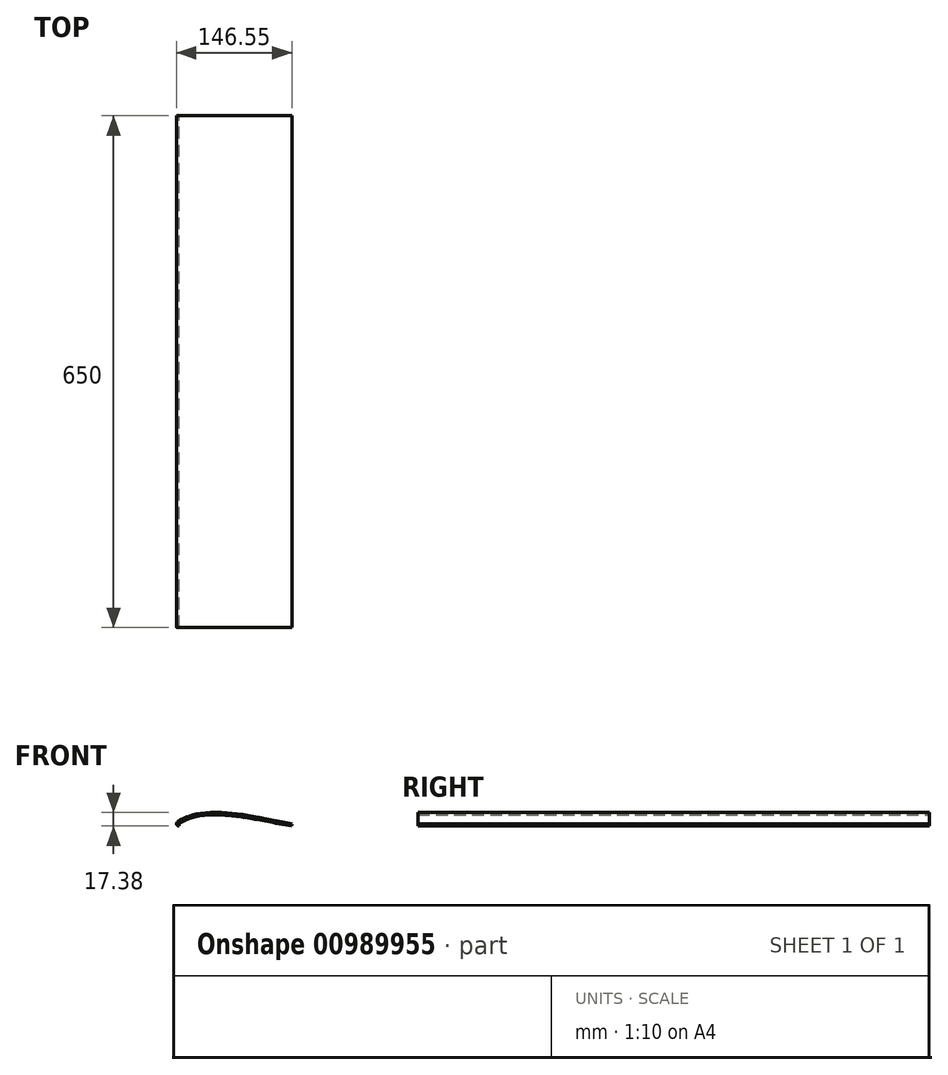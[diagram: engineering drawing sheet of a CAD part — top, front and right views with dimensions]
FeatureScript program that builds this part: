
annotation { "Feature Type Name" : "Feature", "Feature Type Description" : "" }
export const myFeature = defineFeature(function(context is Context, id is Id, definition is map)
    precondition{}
    {
        {
            var Q0;
            Q0=qCreatedBy(makeId("Front.planeOp"),FACE);
            var sketch = newSketch(context, id + "F0", { "sketchPlane" : qUnion([Q0])});
            skLineSegment(sketch, "E0", {"start": v(0, 0) * mm, "end": v(102, 0) * mm});
            skLineSegment(sketch, "E1.bottom", {"start": v(26, 0) * mm, "end": v(69, 0) * mm});
            skLineSegment(sketch, "E1.top", {"start": v(26, 10) * mm, "end": v(69, 10) * mm, "construction": true});
            skLineSegment(sketch, "E1.left", {"start": v(26, 0) * mm, "end": v(26, 10) * mm, "construction": true});
            skLineSegment(sketch, "E1.right", {"start": v(69, 0) * mm, "end": v(69, 10) * mm, "construction": true});
            skLineSegment(sketch, "E2", {"start": v(102, 0) * mm, "end": v(127, 0) * mm});
            skLineSegment(sketch, "E3.bottom", {"start": v(9, 0) * mm, "end": v(26, 0) * mm});
            skLineSegment(sketch, "E3.top", {"start": v(9, 5) * mm, "end": v(26, 5) * mm, "construction": true});
            skLineSegment(sketch, "E3.left", {"start": v(9, 0) * mm, "end": v(9, 5) * mm, "construction": true});
            skLineSegment(sketch, "E3.right", {"start": v(26, 0) * mm, "end": v(26, 5) * mm});
            skFitSpline(sketch, "E4", {"points": [v(0, 0) * mm, v(9, 5) * mm, v(26, 10) * mm, v(69, 10) * mm, v(127, 0) * mm], "startDerivative": vector(100.72, 59.29) * mm, "endDerivative": vector(193.95, -38.05) * mm});
            skLineSegment(sketch, "E5", {"start": v(0, 0) * mm, "end": v(0, -3) * mm});
            skLineSegment(sketch, "E6", {"start": v(0, -3) * mm, "end": v(143, -3) * mm});
            skLineSegment(sketch, "E7", {"start": v(143, -3) * mm, "end": v(127, 0) * mm});
            skLineSegment(sketch, "E8", {"start": v(143, -3) * mm, "end": v(143.55, -0.05) * mm});
            skFitSpline(sketch, "E9", {"points": [v(143.55, -0.05) * mm, v(69.31, 12.98) * mm, v(25.51, 12.96) * mm, v(7.77, 7.74) * mm, v(-1.5, 2.6) * mm], "startDerivative": vector(-307.51, 59.8) * mm, "endDerivative": vector(-155.36, -89.7) * mm});
            skArc(sketch, "E10", {"start": v(-1.5, 2.6) * mm, "mid": v(-2.9, -0.78) * mm, "end": v(0, -3) * mm});
            skLineSegment(sketch, "E11", {"start": v(26, 10) * mm, "end": v(44.77, 13.08) * mm, "construction": true});
            skLineSegment(sketch, "E12", {"start": v(26, 10) * mm, "end": v(25.51, 12.96) * mm, "construction": true});
            skLineSegment(sketch, "E13", {"start": v(9, 5) * mm, "end": v(29.33, 14.1) * mm, "construction": true});
            skLineSegment(sketch, "E14", {"start": v(9, 5) * mm, "end": v(7.77, 7.74) * mm, "construction": true});
            skLineSegment(sketch, "E15", {"start": v(69, 10) * mm, "end": v(167.4, -0.31) * mm, "construction": true});
            skLineSegment(sketch, "E16", {"start": v(69, 10) * mm, "end": v(69.31, 12.98) * mm, "construction": true});
            skLineSegment(sketch, "E17", {"start": v(47.5, 10) * mm, "end": v(47.5, -11.43) * mm, "construction": true});
            skLineSegment(sketch, "E18", {"start": v(47.5, -11.43) * mm, "end": v(-3, -11.43) * mm, "construction": true});
            skLineSegment(sketch, "E19", {"start": v(-3, -11.43) * mm, "end": v(-3, 0) * mm, "construction": true});
            skLineSegment(sketch, "E20", {"start": v(31, 10) * mm, "end": v(31, 0) * mm, "construction": true});
            skLineSegment(sketch, "E21", {"start": v(64, 10) * mm, "end": v(64, 0) * mm, "construction": true});
            skLineSegment(sketch, "E22", {"start": v(-1.5, 2.6) * mm, "end": v(0, 0) * mm, "construction": true});
            skLineSegment(sketch, "E23", {"start": v(0, 0) * mm, "end": v(-2.9, -0.78) * mm, "construction": true});
            skArc(sketch, "E24", {"start": v(-2.9, -0.78) * mm, "mid": v(-1.83, -2.38) * mm, "end": v(0, -3) * mm});
            skCircle(sketch, "E25", {"center": v(60, 4) * mm, "radius": 4 * mm});
            skLineSegment(sketch, "E26", {"start": v(64, 8) * mm, "end": v(56, 8) * mm});
            skLineSegment(sketch, "E27", {"start": v(56, 8) * mm, "end": v(56, 0) * mm});
            skLineSegment(sketch, "E28", {"start": v(56, 8) * mm, "end": v(56, 11.03) * mm});
            skLineSegment(sketch, "E29", {"start": v(56, 11.03) * mm, "end": v(64, 10) * mm});
            skLineSegment(sketch, "E30", {"start": v(51, 0) * mm, "end": v(51, 11.03) * mm});
            skLineSegment(sketch, "E31", {"start": v(51, 11.03) * mm, "end": v(56, 11.03) * mm});
            skSolve(sketch);
        }
        {
            var Q0;
            Q0=makeQuery(id+"F0.imprint","IMPRINT",FACE,{"disambiguationData":[TD([[makeQuery(id+"F0.imprint","IMPRINT",EDGE,{"derivedFrom":sQuery(id+"F0.wireOp",EDGE,"E4")}),1.0]])]});
            var Q1;
            {var subQ1=sQuery(id+"F0.wireOp",EDGE,"E1.bottom");Q1=makeQuery(id+"F0.imprint","IMPRINT",FACE,{"disambiguationData":[TD([[makeQuery(id+"F0.imprint","IMPRINT",EDGE,{"derivedFrom":subQ1}),-1.0]])]});}
            extrude(context, id + "F1", {"entities" : qUnion([Q0, Q1]), "endBound" : BoundingType.SYMMETRIC, "depth" : 650 * mm, "offsetDistance" : 25 * mm});
        }
    });
